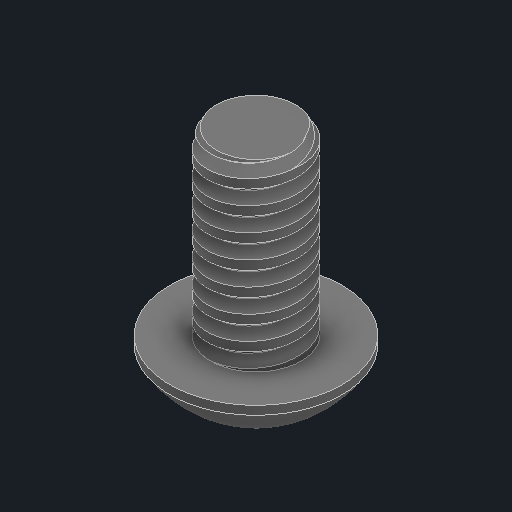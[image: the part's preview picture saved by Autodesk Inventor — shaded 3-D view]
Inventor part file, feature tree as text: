
AUTODESK INVENTOR PART (.ipt)
format: ipt  version: 2025 (Build 290162000, 162)  size: 304,640 bytes
history: native  units: in
note: dims shown in document units (in); Inventor stores cm internally (conversion verified against a paired STEP export)
features: thread x1
ambient origin geometry x8: Origin, YZ Plane, XZ Plane, XY Plane, X Axis, Y Axis, Z Axis, Center Point
bodies: Solid1 (feature_tree)
feature tree (1):
  thread  "THREADS"  [1 undecoded]
note: 1 required parameter value undecoded (feature->parameter linkage not recoverable at this tier; creation-order binding heuristic only, values carry confidence <= 0.55)
